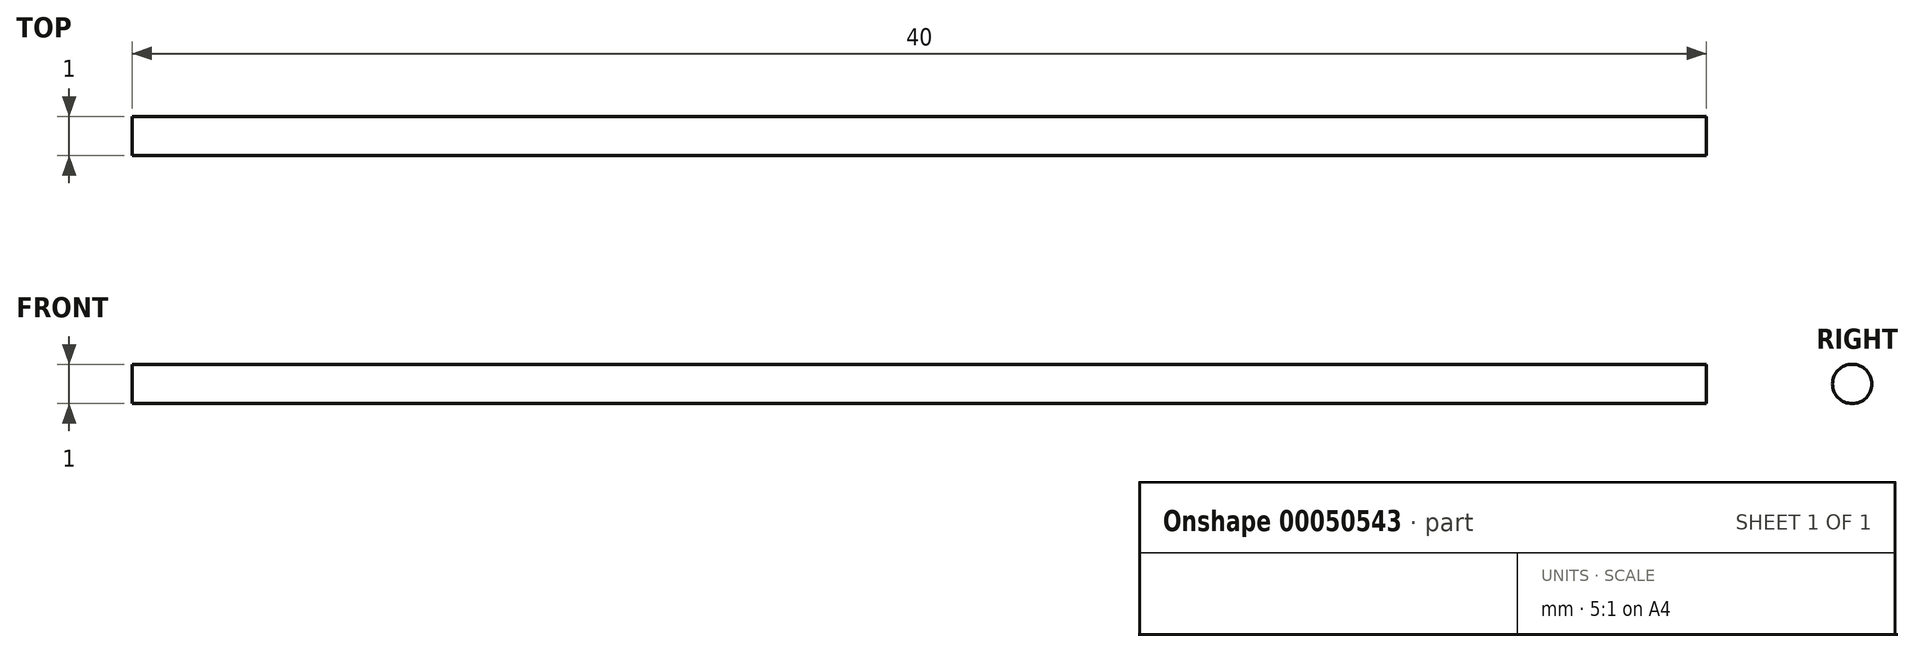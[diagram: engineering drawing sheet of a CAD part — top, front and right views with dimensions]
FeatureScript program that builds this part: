
annotation { "Feature Type Name" : "Feature", "Feature Type Description" : "" }
export const myFeature = defineFeature(function(context is Context, id is Id, definition is map)
    precondition{}
    {
        {
            var Q0;
            Q0=qCreatedBy(makeId("Right.planeOp"),FACE);
            var sketch = newSketch(context, id + "F0", { "sketchPlane" : qUnion([Q0])});
            skCircle(sketch, "E0", {"center": v(0, 0) * mm, "radius": 0.5 * mm});
            skSolve(sketch);
        }
        {
            var Q0;
            Q0 = qSketchRegion(id + "F0", true);
            extrude(context, id + "F1", {"entities" : qUnion([Q0]), "depth" : 40 * mm});
        }
    });
